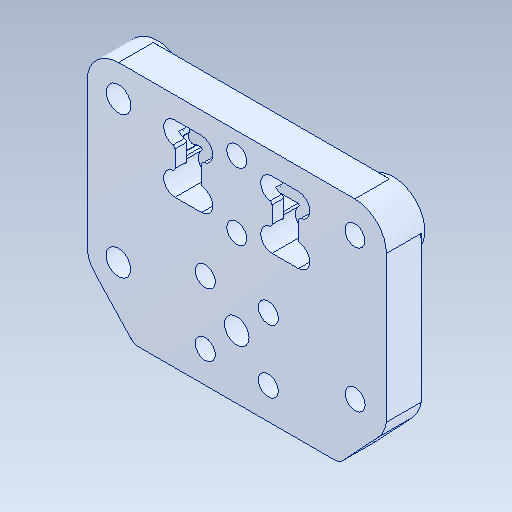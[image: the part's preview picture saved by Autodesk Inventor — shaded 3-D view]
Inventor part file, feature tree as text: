
AUTODESK INVENTOR PART (.ipt)
format: ipt  version: 2020 (Build 240168000, 168)  size: 238,592 bytes
history: native  units: in
note: dims shown in document units (in); Inventor stores cm internally (conversion verified against a paired STEP export)
features: fillet x1
ambient origin geometry x8: Origin, YZ Plane, XZ Plane, XY Plane, X Axis, Y Axis, Z Axis, Center Point
bodies: Solid1 (feature_tree)
feature tree (1):
  fillet  "Fillet9"  [1 undecoded]
note: 1 required parameter value undecoded (feature->parameter linkage not recoverable at this tier; creation-order binding heuristic only, values carry confidence <= 0.55)
